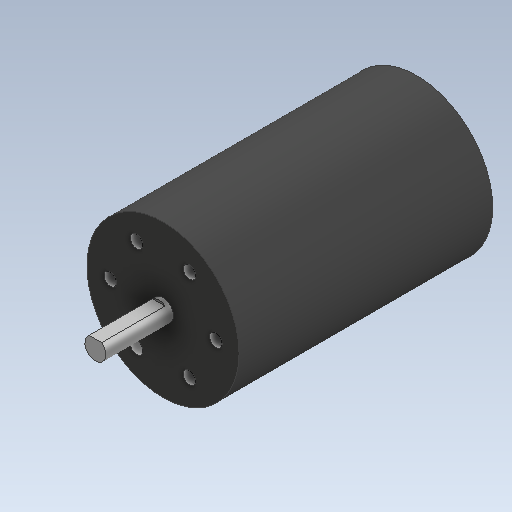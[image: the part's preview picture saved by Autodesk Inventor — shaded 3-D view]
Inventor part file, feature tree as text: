
AUTODESK INVENTOR PART (.ipt)
format: ipt  version: 2021 (Build 250183000, 183)  size: 130,048 bytes
history: native  units: mm
features: extrude x4, sketch x4
ambient origin geometry x8: Origin, YZ Plane, XZ Plane, XY Plane, X Axis, Y Axis, Z Axis, Center Point
bodies: Solid1 (feature_tree)
feature tree (8):
  extrude  "Extrusion1"  Depth=60.0mm TaperAngle=0.0deg
  extrude  "Extrusion2"  Depth=16.0mm TaperAngle=0.0deg
  extrude  "Extrusion3"  Depth=15.0mm TaperAngle=0.0deg
  extrude  "Extrusion4"  Depth=10.0mm
  sketch  "Sketch1"  dims[d0=36.0mm d1=60.0mm d2=0.0mm]
  sketch  "Sketch2"  dims[d3=5.0mm d4=16.0mm d5=0.0mm]
  sketch  "Sketch3"  dims[d6=4.5mm d7=15.0mm d8=0.0mm]
  sketch  "Sketch4"  dims[d9=3.0mm d10=12.5mm d11=60.0mm d13=360.0deg d15=10.0mm d16=0.0mm]
